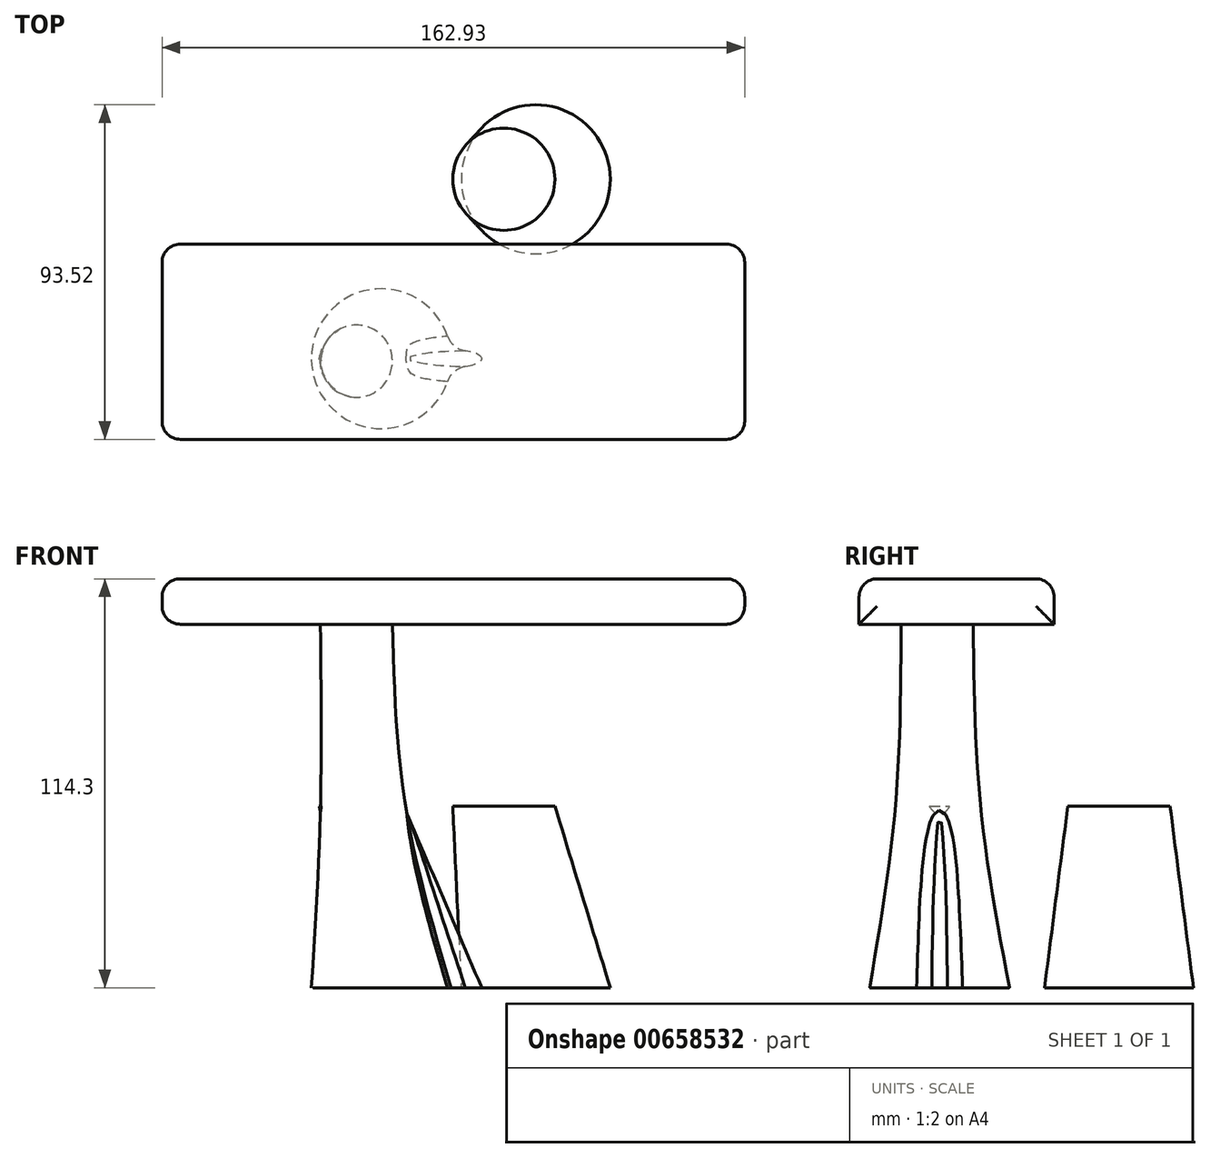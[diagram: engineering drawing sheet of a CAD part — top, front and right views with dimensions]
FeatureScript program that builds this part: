
annotation { "Feature Type Name" : "Feature", "Feature Type Description" : "" }
export const myFeature = defineFeature(function(context is Context, id is Id, definition is map)
    precondition{}
    {
        {
            var Q0;
            Q0=qCreatedBy(makeId("Top.planeOp"),FACE);
            var sketch = newSketch(context, id + "F0", { "sketchPlane" : qUnion([Q0])});
            skCircle(sketch, "E0", {"center": v(0, 0) * mm, "radius": 14.29 * mm});
            skSolve(sketch);
        }
        {
            var Q0;
            Q0=qCreatedBy(makeId("Top.planeOp"),FACE);
            cPlane(context, id + "F1", {"entities" : qUnion([Q0]), "cplaneType" : CPlaneType.OFFSET, "offset" : 50.8 * mm, "oppositeDirection" : true, "width" : 152.4 * mm, "height" : 152.4 * mm});
        }
        {
            var Q0;
            Q0=qCreatedBy(id+"F1.planeOp",FACE);
            var sketch = newSketch(context, id + "F2", { "sketchPlane" : qUnion([Q0])});
            skCircle(sketch, "E1", {"center": v(8.94, 0) * mm, "radius": 20.83 * mm});
            skSolve(sketch);
        }
        {
            var Q0;
            Q0=makeQuery(id+"F2.imprint","IMPRINT",FACE,{"disambiguationData":[TD([[makeQuery(id+"F2.imprint","IMPRINT",EDGE,{"derivedFrom":sQuery(id+"F2.wireOp",EDGE,"E1")}),1.0]])]});
            var Q1;
            Q1=makeQuery(id+"F0.imprint","IMPRINT",FACE,{"disambiguationData":[TD([[makeQuery(id+"F0.imprint","IMPRINT",EDGE,{"derivedFrom":sQuery(id+"F0.wireOp",EDGE,"E0")}),1.0]])]});
            loft(context, id + "F3", {"sheetProfilesArray" : [{ "sheetProfileEntities" : qUnion([Q0]) }, { "sheetProfileEntities" : qUnion([Q1]) }]});
        }
        {
            var Q0;
            Q0=qCreatedBy(id+"F1.planeOp",FACE);
            cPlane(context, id + "F4", {"entities" : qUnion([Q0]), "cplaneType" : CPlaneType.OFFSET, "offset" : 101.6 * mm, "width" : 152.4 * mm, "height" : 152.4 * mm});
        }
        {
            var Q0;
            Q0=qCreatedBy(id+"F1.planeOp",FACE);
            var sketch = newSketch(context, id + "F5", { "sketchPlane" : qUnion([Q0])});
            skCircle(sketch, "E2", {"center": v(-34.26, -50.17) * mm, "radius": 19.56 * mm});
            skSolve(sketch);
        }
        {
            var Q0;
            Q0=qCreatedBy(makeId("Top.planeOp"),FACE);
            var sketch = newSketch(context, id + "F6", { "sketchPlane" : qUnion([Q0])});
            skCircle(sketch, "E3", {"center": v(-39.37, -50.63) * mm, "radius": 11.9 * mm});
            skSolve(sketch);
        }
        {
            var Q0;
            Q0=qCreatedBy(id+"F4.planeOp",FACE);
            var sketch = newSketch(context, id + "F7", { "sketchPlane" : qUnion([Q0])});
            skCircle(sketch, "E4", {"center": v(-41.22, -50.86) * mm, "radius": 10.08 * mm});
            skSolve(sketch);
        }
        {
            var Q0;
            Q0=makeQuery(id+"F5.imprint","IMPRINT",FACE,{"disambiguationData":[TD([[makeQuery(id+"F5.imprint","IMPRINT",EDGE,{"derivedFrom":sQuery(id+"F5.wireOp",EDGE,"E2")}),1.0]])]});
            var Q1;
            Q1=makeQuery(id+"F6.imprint","IMPRINT",FACE,{"disambiguationData":[TD([[makeQuery(id+"F6.imprint","IMPRINT",EDGE,{"derivedFrom":sQuery(id+"F6.wireOp",EDGE,"E3")}),1.0]])]});
            var Q2;
            Q2=makeQuery(id+"F7.imprint","IMPRINT",FACE,{"disambiguationData":[TD([[makeQuery(id+"F7.imprint","IMPRINT",EDGE,{"derivedFrom":sQuery(id+"F7.wireOp",EDGE,"E4")}),1.0]])]});
            loft(context, id + "F8", {"sheetProfilesArray" : [{ "sheetProfileEntities" : qUnion([Q0]) }, { "sheetProfileEntities" : qUnion([Q1]) }, { "sheetProfileEntities" : qUnion([Q2]) }]});
        }
        {
            var Q0;
            Q0=qCreatedBy(id+"F1.planeOp",FACE);
            var sketch = newSketch(context, id + "F9", { "sketchPlane" : qUnion([Q0])});
            skEllipse(sketch, "E5", {"center": v(-18.23, -50.17) * mm, "majorRadius": 12.08 * mm, "minorRadius": 2.8 * mm, "majorAxis": v(1, 0)});
            skSolve(sketch);
        }
        {
            var Q0;
            Q0=qCreatedBy(makeId("Top.planeOp"),FACE);
            var sketch = newSketch(context, id + "F10", { "sketchPlane" : qUnion([Q0])});
            skEllipse(sketch, "E6", {"center": v(-39.83, -50.17) * mm, "majorRadius": 11.84 * mm, "minorRadius": 3.28 * mm, "majorAxis": v(1, 0)});
            skSolve(sketch);
        }
        {
            var Q1;
            Q1 = qSketchRegion(id + "F9", true);
            var Q2;
            Q2 = qSketchRegion(id + "F10", true);
            loft(context, id + "F11", {"operationType" : NewBodyOperationType.ADD, "sheetProfilesArray" : [{ "sheetProfileEntities" : qUnion([Q1]) }, { "sheetProfileEntities" : qUnion([Q2]) }]});
        }
        {
            var Q0;
            Q0=makeQuery(id+"F11.boolean.opBoolean","INTERSECT",EDGE,{"disambiguationData":[OD(0.0)],"derivedFrom":[makeQuery(id+"F8.opLoft","SWEPT_FACE",FACE,{"disambiguationData":[OSD([sQuery(id+"F5.wireOp",EDGE,"E2"),sQuery(id+"F6.wireOp",EDGE,"E3")])]}),makeQuery(id+"F11.opLoft","SWEPT_FACE",FACE,{"disambiguationData":[OSD([sQuery(id+"F9.wireOp",EDGE,"E5"),sQuery(id+"F10.wireOp",EDGE,"E6")])]})]});
            fillet(context, id + "F12", {"entities" : qUnion([Q0]), "radius" : 6.35 * mm, "tangentPropagation" : true, "allowEdgeOverflow" : false});
        }
        {
            var Q0;
            Q0=makeQuery(id+"F8.opLoft","CAP_FACE",FACE,{"disambiguationData":[OSD([makeQuery(id+"F7.imprint","IMPRINT",FACE,{"disambiguationData":[TD([[makeQuery(id+"F7.imprint","IMPRINT",EDGE,{"derivedFrom":sQuery(id+"F7.wireOp",EDGE,"E4")}),1.0]])]})])],"isStart":true});
            var sketch = newSketch(context, id + "F13", { "sketchPlane" : qUnion([Q0])});
            skLineSegment(sketch, "E7.bottom", {"start": v(-95.57, -18.15) * mm, "end": v(67.36, -18.15) * mm});
            skLineSegment(sketch, "E7.top", {"start": v(-95.57, -72.7) * mm, "end": v(67.36, -72.7) * mm});
            skLineSegment(sketch, "E7.left", {"start": v(-95.57, -18.15) * mm, "end": v(-95.57, -72.7) * mm});
            skLineSegment(sketch, "E7.right", {"start": v(67.36, -18.15) * mm, "end": v(67.36, -72.7) * mm});
            skSolve(sketch);
        }
        {
            var Q0;
            Q0 = qSketchRegion(id + "F13", true);
            extrude(context, id + "F14", {"entities" : qUnion([Q0]), "operationType" : NewBodyOperationType.ADD, "depth" : 12.7 * mm, "offsetDistance" : 25.4 * mm});
        }
        {
            var Q0;
            Q0=makeQuery(id+"F14.opExtrude","CAP_FACE",FACE,{"disambiguationData":[OSD([sQuery(id+"F13.wireOp",EDGE,"E7.bottom"),sQuery(id+"F13.wireOp",EDGE,"E7.top"),sQuery(id+"F13.wireOp",EDGE,"E7.left"),sQuery(id+"F13.wireOp",EDGE,"E7.right")])],"isStart":false});
            fillet(context, id + "F15", {"entities" : qUnion([Q0]), "radius" : 5.08 * mm, "tangentPropagation" : true, "allowEdgeOverflow" : false});
        }
        {
            var Q0;
            Q0=makeQuery(id+"F14.opExtrude","SWEPT_FACE",FACE,{"disambiguationData":[OSD([sQuery(id+"F13.wireOp",EDGE,"E7.right")])]});
            var Q1;
            Q1=makeQuery(id+"F14.opExtrude","SWEPT_FACE",FACE,{"disambiguationData":[OSD([sQuery(id+"F13.wireOp",EDGE,"E7.left")])]});
            fillet(context, id + "F16", {"entities" : qUnion([Q0, Q1]), "radius" : 5.08 * mm, "tangentPropagation" : true, "allowEdgeOverflow" : false});
        }
    });
